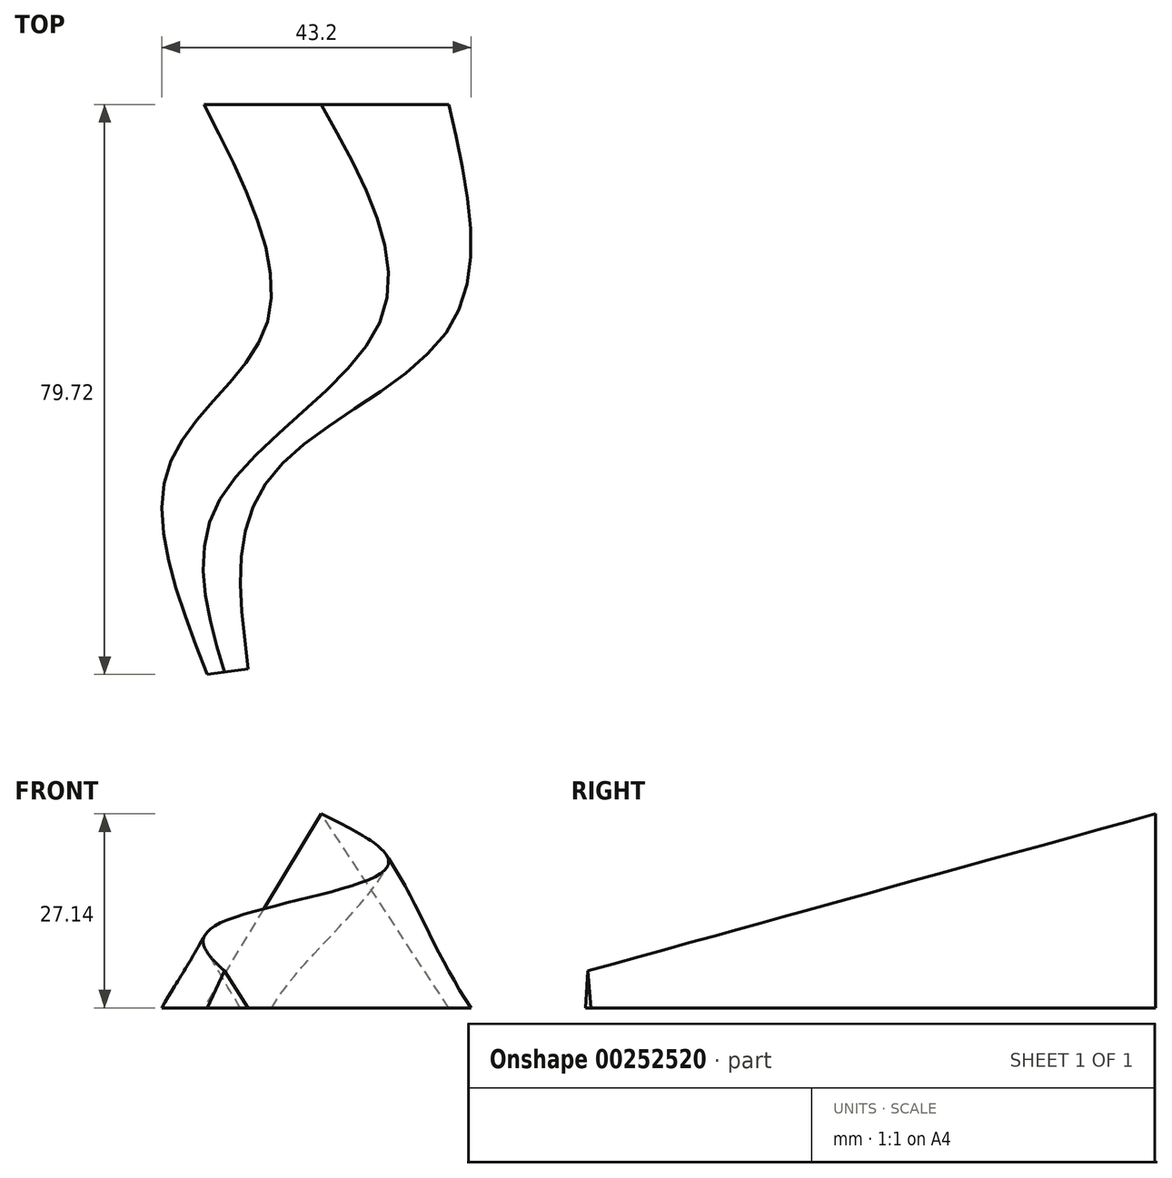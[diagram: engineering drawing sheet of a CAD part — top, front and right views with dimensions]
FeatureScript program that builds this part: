
annotation { "Feature Type Name" : "Feature", "Feature Type Description" : "" }
export const myFeature = defineFeature(function(context is Context, id is Id, definition is map)
    precondition{}
    {
        {
            var Q0;
            Q0=qCreatedBy(makeId("Front.planeOp"),FACE);
            var sketch = newSketch(context, id + "F0", { "sketchPlane" : qUnion([Q0])});
            skLineSegment(sketch, "E0", {"start": v(-16.4, 0) * mm, "end": v(17.85, 0) * mm});
            skLineSegment(sketch, "E1", {"start": v(17.85, 0) * mm, "end": v(0, 27.14) * mm});
            skLineSegment(sketch, "E2", {"start": v(0, 27.14) * mm, "end": v(-16.4, 0) * mm});
            skLineSegment(sketch, "E3", {"start": v(0, 27.14) * mm, "end": v(10.3, 27.14) * mm});
            skSolve(sketch);
        }
        {
            var Q0;
            Q0=qCreatedBy(makeId("Top.planeOp"),FACE);
            var sketch = newSketch(context, id + "F1", { "sketchPlane" : qUnion([Q0])});
            skFitSpline(sketch, "E4", {"points": [v(-16.4, 0) * mm, v(-7.6, -30.74) * mm, v(-21.2, -50.32) * mm, v(-15.93, -79.72) * mm], "startDerivative": vector(48.86, -94.91) * mm, "endDerivative": vector(36.68, -93.67) * mm});
            skPoint(sketch, "E5.0", {"position": v(17.85, 0) * mm});
            skFitSpline(sketch, "E6", {"points": [v(17.85, 0) * mm, v(17.85, -31.34) * mm, v(-7.42, -52.55) * mm, v(-10.19, -78.94) * mm], "startDerivative": vector(23.63, -102.3) * mm, "endDerivative": vector(11.93, -92.5) * mm});
            skLineSegment(sketch, "E7", {"start": v(-15.93, -79.72) * mm, "end": v(-10.19, -78.94) * mm});
            skSolve(sketch);
        }
        {
            var Q0;
            Q0=sQuery(id+"F1.wireOp",EDGE,"E7");
            cPlane(context, id + "F2", {"entities" : qUnion([Q0]), "cplaneType" : CPlaneType.LINE_ANGLE, "offset" : 25.4 * mm, "angle" : 0 * degree, "width" : 152.4 * mm, "height" : 152.4 * mm});
        }
        {
            var Q0;
            Q0=qCreatedBy(id+"F2.planeOp",FACE);
            var sketch = newSketch(context, id + "F3", { "sketchPlane" : qUnion([Q0])});
            skLineSegment(sketch, "E8.0", {"start": v(26.43, 0) * mm, "end": v(20.64, 0) * mm});
            skLineSegment(sketch, "E9", {"start": v(26.43, 0) * mm, "end": v(24.03, 5.17) * mm});
            skLineSegment(sketch, "E10", {"start": v(24.03, 5.17) * mm, "end": v(20.64, 0) * mm});
            skSolve(sketch);
        }
        {
            var Q0;
            Q0=sQuery(id+"F0.wireOp",VERTEX,"E3.start");
            var Q1;
            Q1=sQuery(id+"F0.wireOp",VERTEX,"E3.end");
            var Q2;
            Q2=sQuery(id+"F3.wireOp",VERTEX,"E9.end");
            cPlane(context, id + "F4", {"entities" : qUnion([Q0, Q1, Q2]), "cplaneType" : CPlaneType.THREE_POINT, "offset" : 25.4 * mm, "width" : 152.4 * mm, "height" : 152.4 * mm});
        }
        {
            var Q0;
            Q0=qCreatedBy(id+"F4.planeOp",FACE);
            var sketch = newSketch(context, id + "F5", { "sketchPlane" : qUnion([Q0])});
            skPoint(sketch, "E11.0", {"position": v(0, 7.24) * mm});
            skPoint(sketch, "E11.1", {"position": v(-13.55, -75.14) * mm});
            skFitSpline(sketch, "E12", {"points": [v(0, 7.24) * mm, v(8.34, -24.04) * mm, v(-14.27, -50.3) * mm, v(-13.55, -75.14) * mm], "startDerivative": vector(52.18, -96.2) * mm, "endDerivative": vector(24.18, -85.74) * mm});
            skSolve(sketch);
        }
        {
            var Q0;
            Q0=makeQuery(id+"F0.imprint","IMPRINT",FACE,{"disambiguationData":[TD([[makeQuery(id+"F0.imprint","IMPRINT",EDGE,{"derivedFrom":sQuery(id+"F0.wireOp",EDGE,"E0")}),1.0]])]});
            var Q1;
            Q1=makeQuery(id+"F3.imprint","IMPRINT",FACE,{"disambiguationData":[TD([[makeQuery(id+"F3.imprint","IMPRINT",EDGE,{"derivedFrom":sQuery(id+"F3.wireOp",EDGE,"E8.0")}),-1.0]])]});
            var Q2;
            Q2=sQuery(id+"F1.wireOp",EDGE,"E4");
            var Q3;
            Q3=sQuery(id+"F5.wireOp",EDGE,"E12");
            var Q4;
            Q4=sQuery(id+"F1.wireOp",EDGE,"E6");
            loft(context, id + "F6", {"addGuides" : true, "sheetProfilesArray" : [{ "sheetProfileEntities" : qUnion([Q0]) }, { "sheetProfileEntities" : qUnion([Q1]) }], "guidesArray" : [{ "guideEntities" : qUnion([Q2]), "guideDerivativeType" : LoftGuideDerivativeType.DEFAULT, "guideDerivativeMagnitude" : 1 }, { "guideEntities" : qUnion([Q3]), "guideDerivativeType" : LoftGuideDerivativeType.DEFAULT, "guideDerivativeMagnitude" : 1 }, { "guideEntities" : qUnion([Q4]), "guideDerivativeType" : LoftGuideDerivativeType.DEFAULT, "guideDerivativeMagnitude" : 1 }]});
        }
    });
